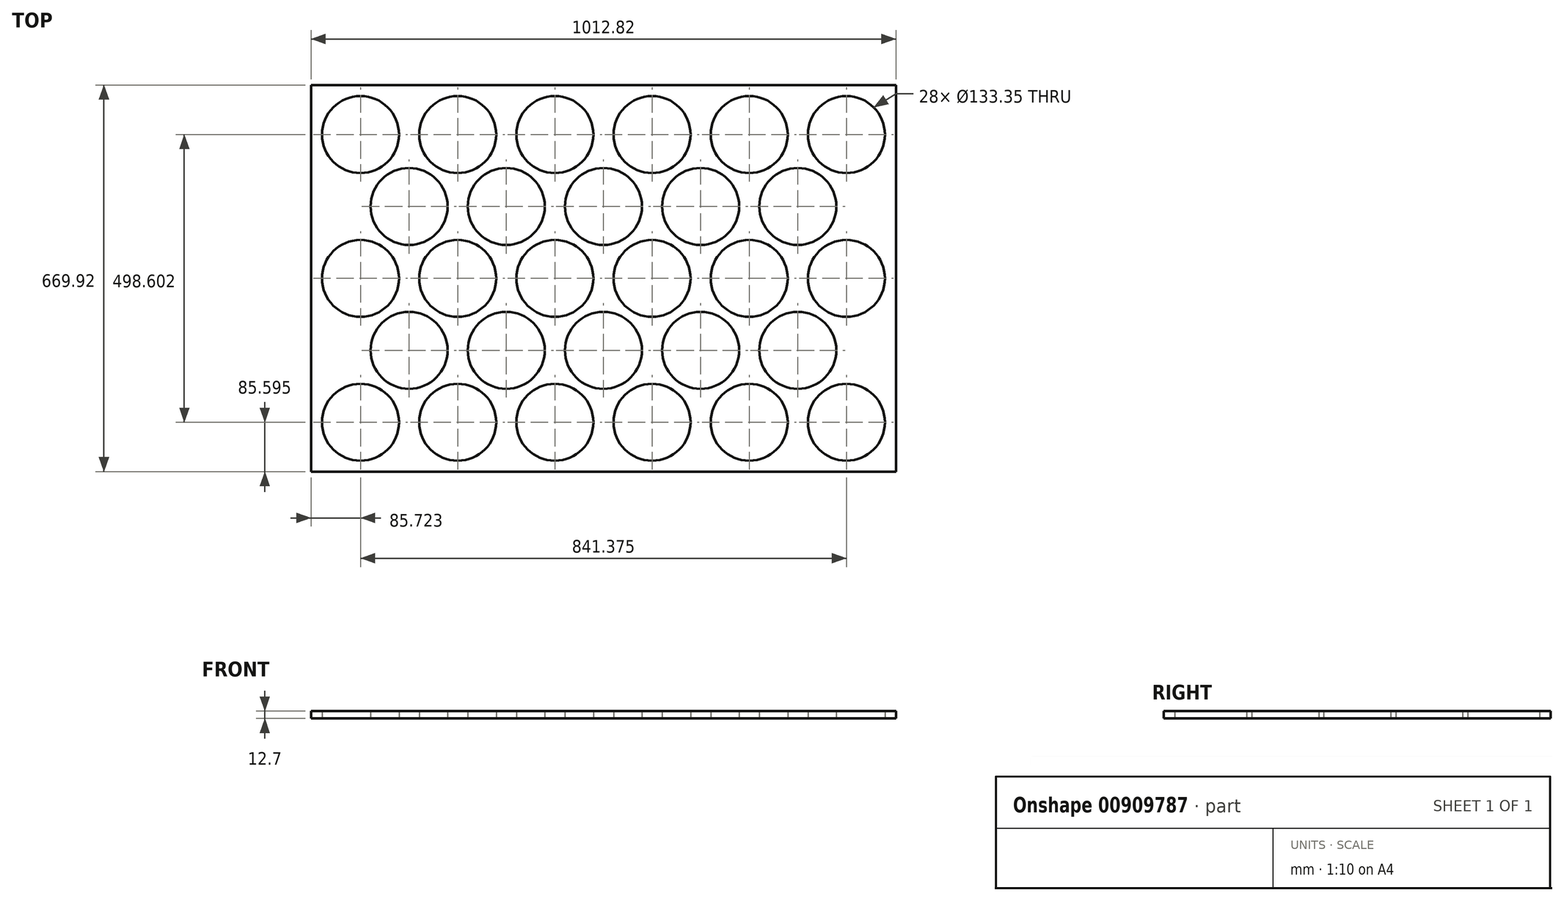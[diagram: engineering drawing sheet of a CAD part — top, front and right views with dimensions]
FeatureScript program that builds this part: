
annotation { "Feature Type Name" : "Feature", "Feature Type Description" : "" }
export const myFeature = defineFeature(function(context is Context, id is Id, definition is map)
    precondition{}
    {
        {
            var Q0;
            Q0=qCreatedBy(makeId("Top.planeOp"),FACE);
            var sketch = newSketch(context, id + "F0", { "sketchPlane" : qUnion([Q0])});
            skLineSegment(sketch, "E0.bottom", {"start": v(-506.41, 334.96) * mm, "end": v(506.41, 334.96) * mm});
            skLineSegment(sketch, "E0.top", {"start": v(-506.41, -334.96) * mm, "end": v(506.41, -334.96) * mm});
            skLineSegment(sketch, "E0.left", {"start": v(-506.41, 334.96) * mm, "end": v(-506.41, -334.96) * mm});
            skLineSegment(sketch, "E0.right", {"start": v(506.41, 334.96) * mm, "end": v(506.41, -334.96) * mm});
            skPoint(sketch, "E0.middle", {"position": v(0, 0) * mm});
            skCircle(sketch, "E1", {"center": v(-420.69, 249.24) * mm, "radius": 66.68 * mm});
            skLineSegment(sketch, "E2", {"start": v(-506.41, -334.96) * mm, "end": v(-506.41, -249.24) * mm, "construction": true});
            skLineSegment(sketch, "E3", {"start": v(-506.41, -249.24) * mm, "end": v(506.41, -249.24) * mm, "construction": true});
            skLineSegment(sketch, "E4", {"start": v(506.41, 334.96) * mm, "end": v(420.69, 334.96) * mm, "construction": true});
            skLineSegment(sketch, "E5", {"start": v(420.69, 334.96) * mm, "end": v(420.69, -249.24) * mm, "construction": true});
            skCircle(sketch, "E6.0.1.0", {"center": v(-420.69, -0.06) * mm, "radius": 66.68 * mm});
            skCircle(sketch, "E6.0.2.0", {"center": v(-420.69, -249.36) * mm, "radius": 66.68 * mm});
            skCircle(sketch, "E6.1.0.0", {"center": v(-252.41, 249.24) * mm, "radius": 66.68 * mm});
            skCircle(sketch, "E6.1.1.0", {"center": v(-252.41, -0.06) * mm, "radius": 66.68 * mm});
            skCircle(sketch, "E6.1.2.0", {"center": v(-252.41, -249.36) * mm, "radius": 66.68 * mm});
            skCircle(sketch, "E6.2.0.0", {"center": v(-84.14, 249.24) * mm, "radius": 66.68 * mm});
            skCircle(sketch, "E6.2.1.0", {"center": v(-84.14, -0.06) * mm, "radius": 66.68 * mm});
            skCircle(sketch, "E6.2.2.0", {"center": v(-84.14, -249.36) * mm, "radius": 66.68 * mm});
            skCircle(sketch, "E6.3.0.0", {"center": v(84.14, 249.24) * mm, "radius": 66.68 * mm});
            skCircle(sketch, "E6.3.1.0", {"center": v(84.14, -0.06) * mm, "radius": 66.68 * mm});
            skCircle(sketch, "E6.3.2.0", {"center": v(84.14, -249.36) * mm, "radius": 66.68 * mm});
            skCircle(sketch, "E6.4.0.0", {"center": v(252.41, 249.24) * mm, "radius": 66.68 * mm});
            skCircle(sketch, "E6.4.1.0", {"center": v(252.41, -0.06) * mm, "radius": 66.68 * mm});
            skCircle(sketch, "E6.4.2.0", {"center": v(252.41, -249.36) * mm, "radius": 66.68 * mm});
            skCircle(sketch, "E6.5.0.0", {"center": v(420.69, 249.24) * mm, "radius": 66.68 * mm});
            skCircle(sketch, "E6.5.1.0", {"center": v(420.69, -0.06) * mm, "radius": 66.68 * mm});
            skCircle(sketch, "E6.5.2.0", {"center": v(420.69, -249.36) * mm, "radius": 66.68 * mm});
            skLineSegment(sketch, "E6.direction1", {"start": v(-420.69, 249.24) * mm, "end": v(-252.41, 249.24) * mm, "construction": true});
            skLineSegment(sketch, "E6.direction2", {"start": v(-420.69, 249.24) * mm, "end": v(-420.69, -0.06) * mm, "construction": true});
            skLineSegment(sketch, "E7", {"start": v(-336.55, 249.24) * mm, "end": v(-336.55, 124.59) * mm, "construction": true});
            skCircle(sketch, "E8", {"center": v(-336.55, 124.59) * mm, "radius": 66.68 * mm});
            skCircle(sketch, "E9.0.1.0", {"center": v(-336.55, -124.71) * mm, "radius": 66.68 * mm});
            skCircle(sketch, "E9.1.0.0", {"center": v(-168.28, 124.59) * mm, "radius": 66.68 * mm});
            skCircle(sketch, "E9.1.1.0", {"center": v(-168.28, -124.71) * mm, "radius": 66.68 * mm});
            skCircle(sketch, "E9.2.0.0", {"center": v(0, 124.59) * mm, "radius": 66.68 * mm});
            skCircle(sketch, "E9.2.1.0", {"center": v(0, -124.71) * mm, "radius": 66.68 * mm});
            skCircle(sketch, "E9.3.0.0", {"center": v(168.28, 124.59) * mm, "radius": 66.68 * mm});
            skCircle(sketch, "E9.3.1.0", {"center": v(168.28, -124.71) * mm, "radius": 66.68 * mm});
            skCircle(sketch, "E9.4.0.0", {"center": v(336.55, 124.59) * mm, "radius": 66.68 * mm});
            skCircle(sketch, "E9.4.1.0", {"center": v(336.55, -124.71) * mm, "radius": 66.68 * mm});
            skLineSegment(sketch, "E9.direction1", {"start": v(-336.55, 124.59) * mm, "end": v(-168.28, 124.59) * mm, "construction": true});
            skLineSegment(sketch, "E9.direction2", {"start": v(-336.55, 124.59) * mm, "end": v(-336.55, -124.71) * mm, "construction": true});
            skSolve(sketch);
        }
        {
            var Q0;
            Q0=qSketchRegion(id+"F0",true);
            extrude(context, id + "F1", {"entities" : qUnion([Q0]), "depth" : 12.7 * mm, "offsetDistance" : 25.4 * mm});
        }
    });
